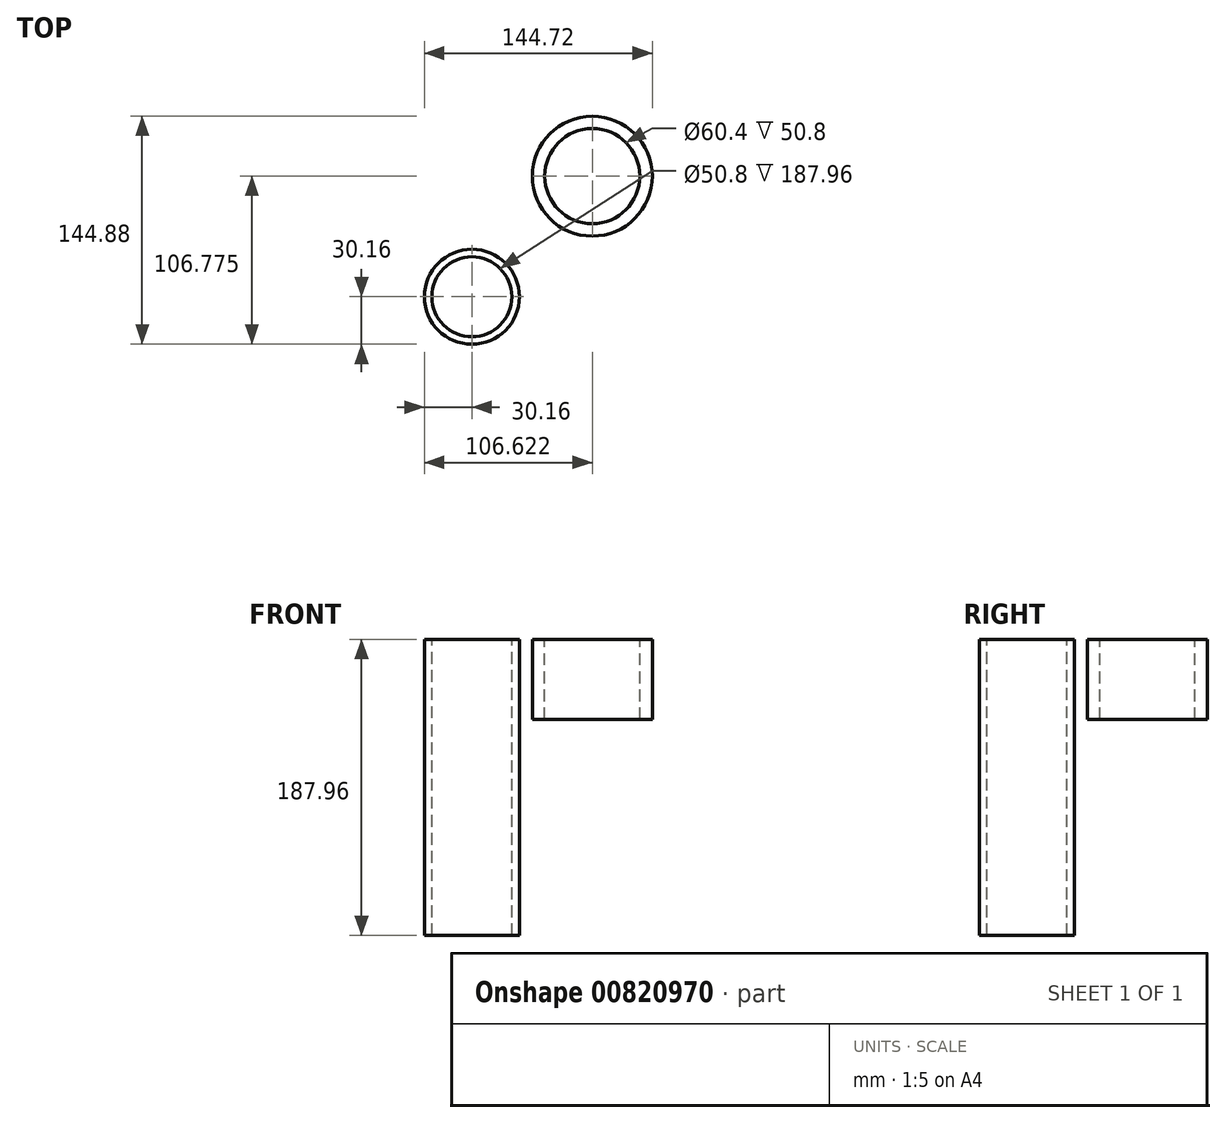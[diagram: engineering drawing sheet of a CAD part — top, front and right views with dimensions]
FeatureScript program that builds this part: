
annotation { "Feature Type Name" : "Feature", "Feature Type Description" : "" }
export const myFeature = defineFeature(function(context is Context, id is Id, definition is map)
    precondition{}
    {
        {
            var Q0;
            Q0=qCreatedBy(makeId("Top.planeOp"),FACE);
            var sketch = newSketch(context, id + "F0", { "sketchPlane" : qUnion([Q0])});
            skCircle(sketch, "E0", {"center": v(0, 0) * mm, "radius": 30.16 * mm});
            skCircle(sketch, "E1", {"center": v(0, 0) * mm, "radius": 25.4 * mm});
            skSolve(sketch);
        }
        {
            var Q0;
            Q0 = qSketchRegion(id + "F0", true);
            extrude(context, id + "F1", {"entities" : qUnion([Q0]), "oppositeDirection" : true, "depth" : 187.96 * mm, "offsetDistance" : 25.4 * mm});
        }
        {
            var Q0;
            Q0=qCreatedBy(makeId("Top.planeOp"),FACE);
            var sketch = newSketch(context, id + "F2", { "sketchPlane" : qUnion([Q0])});
            skCircle(sketch, "E2", {"center": v(76.46, 76.62) * mm, "radius": 38.1 * mm});
            skCircle(sketch, "E3", {"center": v(76.46, 76.62) * mm, "radius": 30.2 * mm});
            skSolve(sketch);
        }
        {
            var Q0;
            Q0 = qSketchRegion(id + "F2", true);
            extrude(context, id + "F3", {"entities" : qUnion([Q0]), "oppositeDirection" : true, "depth" : 50.8 * mm, "offsetDistance" : 25.4 * mm});
        }
    });
